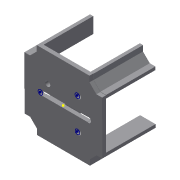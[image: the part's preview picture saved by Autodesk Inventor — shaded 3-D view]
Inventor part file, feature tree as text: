
AUTODESK INVENTOR PART (.ipt)
format: ipt  version: 2022 (Build 260153000, 153)  size: 273,408 bytes
history: native  units: mm
features: plane x7, sketch x7, extrude x5, projected_geometry x2, hole x1
ambient origin geometry x8: Origin, YZ Plane, XZ Plane, XY Plane, X Axis, Y Axis, Z Axis, Center Point
bodies: Body1 (feature_tree)
feature tree (22):
  plane  "Work Plane1"
  plane  "Work Plane2"
  plane  "Work Plane4"
  extrude  "Extrusion1"  Depth=24.9mm
  hole  "Hole1"  [1 undecoded]
  extrude  "IM_offset"  Depth=1.0mm TaperAngle=0.0deg
  extrude  "Extrusion6"  Depth=0.2mm
  plane  "Work Plane3"
  sketch  "Sketch9"  dims[d26=1.0mm d27=0.0mm d28=2.9mm]
  plane  "Work Plane5"
  extrude  "Extrusion9"  Depth=2.9mm
  plane  "Work Plane6"
  sketch  "Sketch11"  dims[d29=10.0mm d30=0.0mm d44=2.0mm]
  plane  "Work Plane7"
  extrude  "Extrusion11"  Depth=2.0mm
  sketch  "Sketch12"  dims[d45=40.0mm d47=360.0deg d49=10.0mm d50=0.0mm d53=10.0mm d54=0.0mm]
  sketch  "Sketch1"  dims[d0=45.0deg d2=24.9mm]
  sketch  "Sketch5"  dims[d3=3.14mm d4=26.9mm]
  sketch  "Skizze6"  dims[d5=20.0mm d6=1.0mm d7=0.0mm]
  projected_geometry  "Projizierte Kontur2"
  sketch  "Sketch7"  dims[d18=3.3mm d19=6.0mm d20=4.0mm d21=2.0mm d22=90.0deg d23=12.0mm d24=20.594885mm d25=0.2mm]
  projected_geometry  "Projected Loop5"
note: 1 required parameter value undecoded (feature->parameter linkage not recoverable at this tier; creation-order binding heuristic only, values carry confidence <= 0.55)
